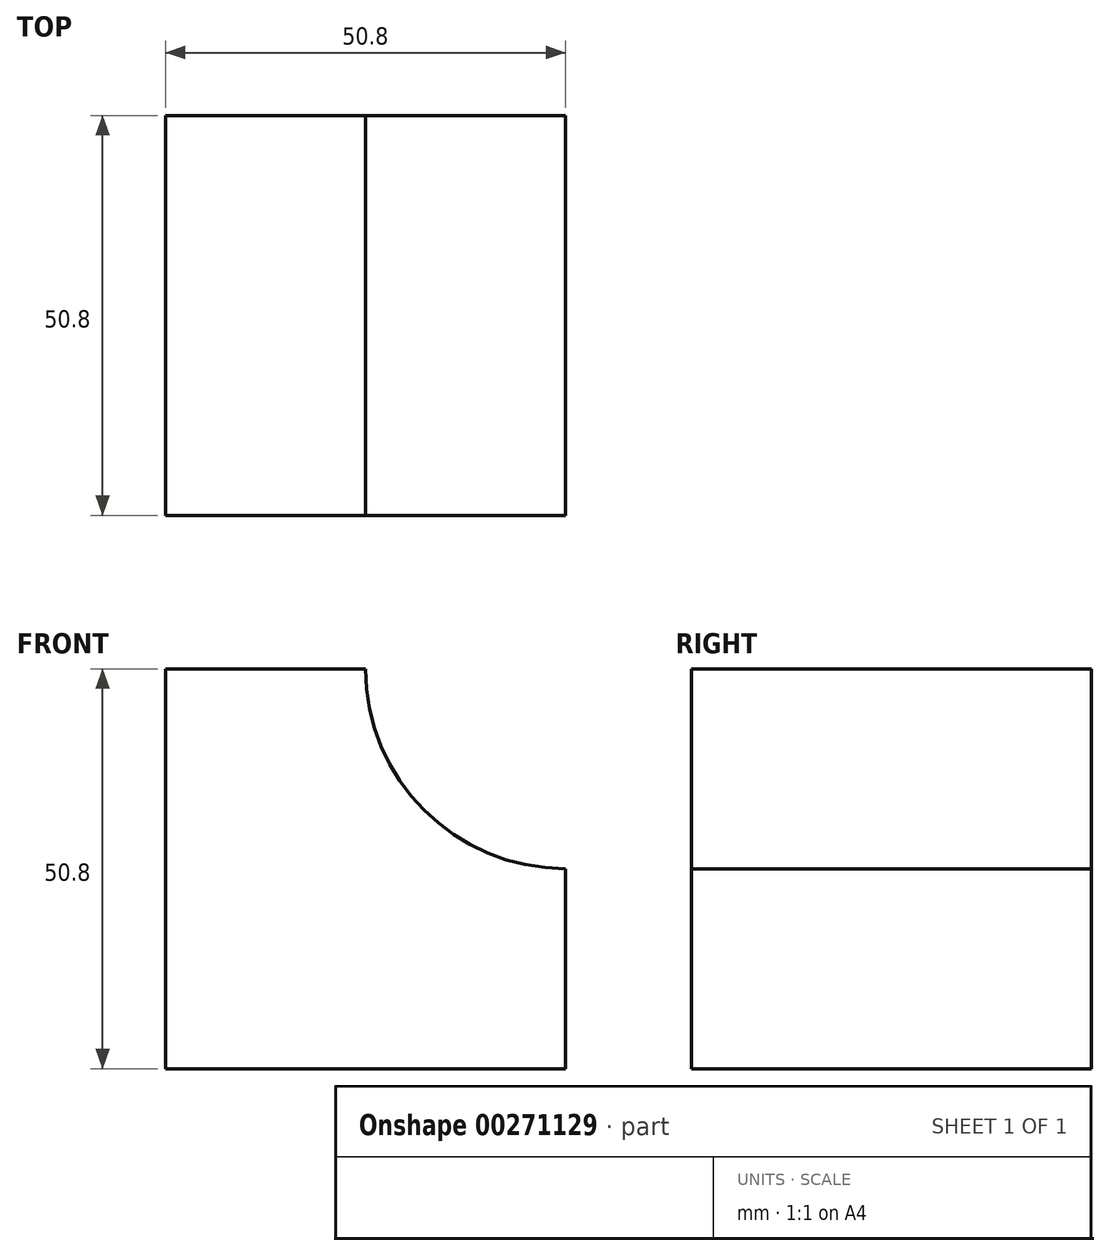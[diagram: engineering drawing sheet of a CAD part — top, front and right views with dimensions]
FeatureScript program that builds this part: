
annotation { "Feature Type Name" : "Feature", "Feature Type Description" : "" }
export const myFeature = defineFeature(function(context is Context, id is Id, definition is map)
    precondition{}
    {
        {
            var Q0;
            Q0=qCreatedBy(makeId("Front.planeOp"),FACE);
            var sketch = newSketch(context, id + "F0", { "sketchPlane" : qUnion([Q0])});
            skLineSegment(sketch, "E0", {"start": v(-38.38, 55) * mm, "end": v(-38.38, 4.2) * mm});
            skLineSegment(sketch, "E1", {"start": v(-38.38, 4.2) * mm, "end": v(12.42, 4.2) * mm});
            skLineSegment(sketch, "E2", {"start": v(12.42, 4.2) * mm, "end": v(12.42, 29.6) * mm});
            skLineSegment(sketch, "E3", {"start": v(-12.98, 55) * mm, "end": v(-38.38, 55) * mm});
            skArc(sketch, "E4", {"start": v(-12.98, 55) * mm, "mid": v(-5.54, 37.04) * mm, "end": v(12.42, 29.6) * mm});
            skSolve(sketch);
        }
        {
            var Q0;
            Q0 = qSketchRegion(id + "F0", true);
            extrude(context, id + "F1", {"entities" : qUnion([Q0]), "depth" : 50.8 * mm});
        }
    });
